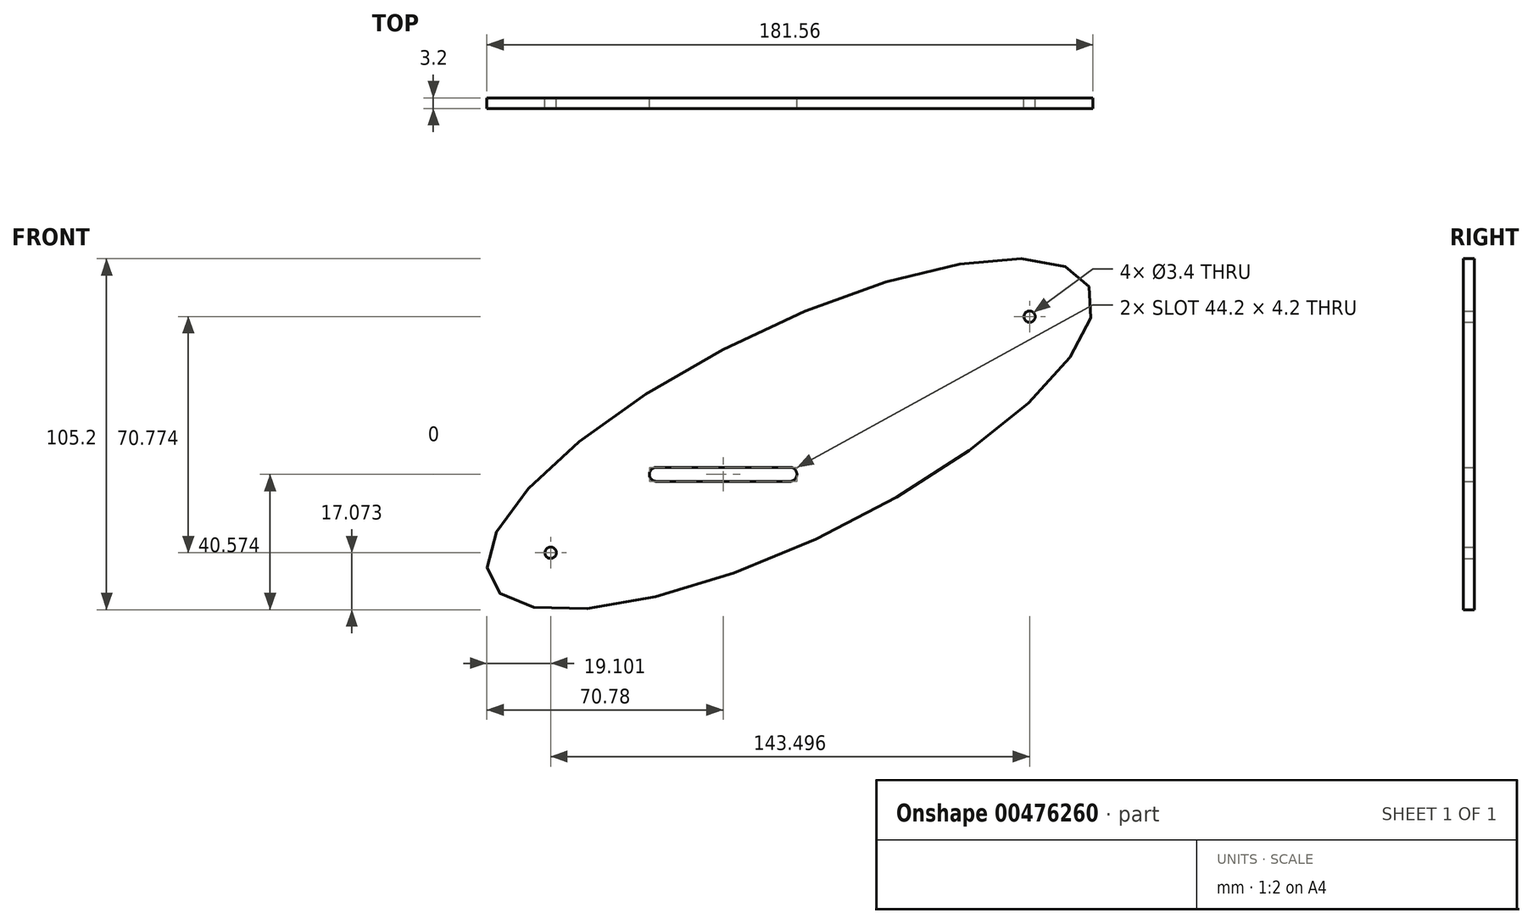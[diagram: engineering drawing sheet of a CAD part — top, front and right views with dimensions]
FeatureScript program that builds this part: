
annotation { "Feature Type Name" : "Feature", "Feature Type Description" : "" }
export const myFeature = defineFeature(function(context is Context, id is Id, definition is map)
    precondition{}
    {
        {
            var Q0;
            Q0=qCreatedBy(makeId("Front.planeOp"),FACE);
            var sketch = newSketch(context, id + "F0", { "sketchPlane" : qUnion([Q0])});
            skEllipse(sketch, "E0", {"center": v(0, 0) * mm, "majorRadius": 100 * mm, "minorRadius": 31.74 * mm, "majorAxis": v(0.9, 0.44)});
            skCircle(sketch, "E1", {"center": v(-71.68, -35.53) * mm, "radius": 1.7 * mm});
            skLineSegment(sketch, "E2", {"start": v(-14.04, 28.47) * mm, "end": v(14.04, -28.47) * mm});
            skCircle(sketch, "E3.MirrorC", {"center": v(71.82, 35.25) * mm, "radius": 1.7 * mm});
            skCircle(sketch, "E4", {"center": v(-40, -12.03) * mm, "radius": 2.1 * mm});
            skLineSegment(sketch, "E5", {"start": v(-40, -9.93) * mm, "end": v(0, -9.93) * mm});
            skLineSegment(sketch, "E6", {"start": v(0, -9.93) * mm, "end": v(0, -14.13) * mm});
            skLineSegment(sketch, "E7", {"start": v(0, -14.13) * mm, "end": v(-40, -14.13) * mm});
            skCircle(sketch, "E8", {"center": v(0, -12.03) * mm, "radius": 2.1 * mm});
            skLineSegment(sketch, "E9", {"start": v(-40, -9.93) * mm, "end": v(-40, -12.03) * mm});
            skLineSegment(sketch, "E10", {"start": v(-40, -14.13) * mm, "end": v(-40, -12.03) * mm});
            skSolve(sketch);
        }
        {
            var Q0;
            Q0=makeQuery(id+"F0.imprint","IMPRINT",FACE,{"disambiguationData":[TD([[makeQuery(id+"F0.imprint","IMPRINT",EDGE,{"derivedFrom":sQuery(id+"F0.wireOp",EDGE,"E0")}),1.0]])]});
            var Q1;
            Q1=makeQuery(id+"F0.imprint","IMPRINT",FACE,{"disambiguationData":[TD([[makeQuery(id+"F0.imprint","IMPRINT",EDGE,{"derivedFrom":sQuery(id+"F0.wireOp",EDGE,"E1")}),-1.0]])]});
            extrude(context, id + "F1", {"entities" : qUnion([Q0, Q1]), "depth" : 3.2 * mm, "offsetDistance" : 25 * mm});
        }
        {
            var Q0;
            Q0=makeQuery(id+"F1.opExtrude","SWEPT_BODY",BODY,{"disambiguationData":[OSD([sQuery(id+"F0.wireOp",EDGE,"E0"),sQuery(id+"F0.wireOp",EDGE,"E1"),sQuery(id+"F0.wireOp",EDGE,"E3.MirrorC")])]});
            transform(context, id + "F2", {"entities" : qUnion([Q0]), "transformType" : TransformType.TRANSLATION_3D, "dx" : 0 * mm, "dy" : 0 * mm, "dz" : 0 * mm, "makeCopy" : true});
        }
    });
